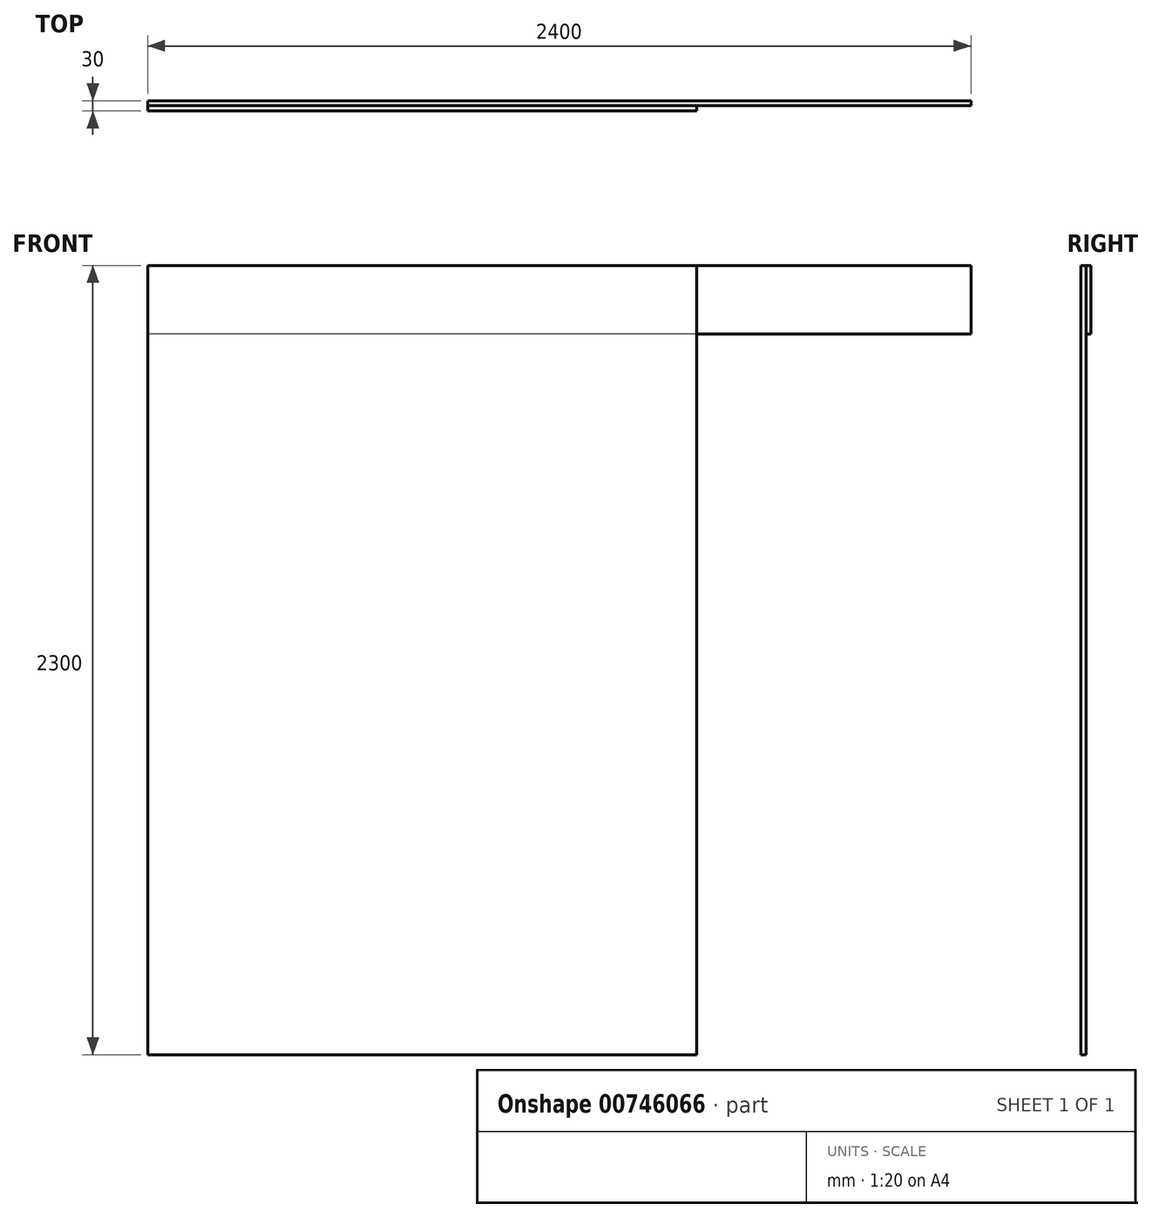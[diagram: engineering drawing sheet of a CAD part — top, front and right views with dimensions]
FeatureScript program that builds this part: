
annotation { "Feature Type Name" : "Feature", "Feature Type Description" : "" }
export const myFeature = defineFeature(function(context is Context, id is Id, definition is map)
    precondition{}
    {
        {
            var Q0;
            Q0=qCreatedBy(makeId("Front.planeOp"),FACE);
            var sketch = newSketch(context, id + "F0", { "sketchPlane" : qUnion([Q0])});
            skLineSegment(sketch, "E0.bottom", {"start": v(0, 0) * mm, "end": v(1600, 0) * mm});
            skLineSegment(sketch, "E0.top", {"start": v(0, 2300) * mm, "end": v(1600, 2300) * mm});
            skLineSegment(sketch, "E0.left", {"start": v(0, 0) * mm, "end": v(0, 2300) * mm});
            skLineSegment(sketch, "E0.right", {"start": v(1600, 0) * mm, "end": v(1600, 2300) * mm});
            skLineSegment(sketch, "E1", {"start": v(0, 2300) * mm, "end": v(2400, 2300) * mm});
            skLineSegment(sketch, "E2", {"start": v(2400, 2300) * mm, "end": v(2400, 2100) * mm});
            skLineSegment(sketch, "E3", {"start": v(2400, 2100) * mm, "end": v(0, 2100) * mm});
            skSolve(sketch);
        }
        {
            var Q0;
            {var subQ0=sQuery(id+"F0.wireOp",EDGE,"E0.bottom");Q0=makeQuery(id+"F0.imprint","IMPRINT",FACE,{"disambiguationData":[TD([[makeQuery(id+"F0.imprint","IMPRINT",EDGE,{"derivedFrom":subQ0}),1.0]])]});}
            var Q1;
            {var subQ0=sQuery(id+"F0.wireOp",EDGE,"E0.top");Q1=makeQuery(id+"F0.imprint","IMPRINT",FACE,{"disambiguationData":[TD([[makeQuery(id+"F0.imprint","IMPRINT",EDGE,{"derivedFrom":subQ0}),-1.0]])]});}
            extrude(context, id + "F1", {"entities" : qUnion([Q0, Q1]), "depth" : 15 * mm, "offsetDistance" : 25 * mm});
        }
        {
            var Q0;
            {var subQ0=sQuery(id+"F0.wireOp",EDGE,"E0.top");Q0=makeQuery(id+"F0.imprint","IMPRINT",FACE,{"disambiguationData":[TD([[makeQuery(id+"F0.imprint","IMPRINT",EDGE,{"derivedFrom":subQ0}),-1.0]])]});}
            var Q1;
            {var subQ0=sQuery(id+"F0.wireOp",EDGE,"E1");Q1=makeQuery(id+"F0.imprint","IMPRINT",FACE,{"disambiguationData":[TD([[makeQuery(id+"F0.imprint","IMPRINT",EDGE,{"derivedFrom":subQ0}),-1.0]])]});}
            extrude(context, id + "F2", {"entities" : qUnion([Q0, Q1]), "oppositeDirection" : true, "depth" : 15 * mm, "offsetDistance" : 25 * mm});
        }
    });
